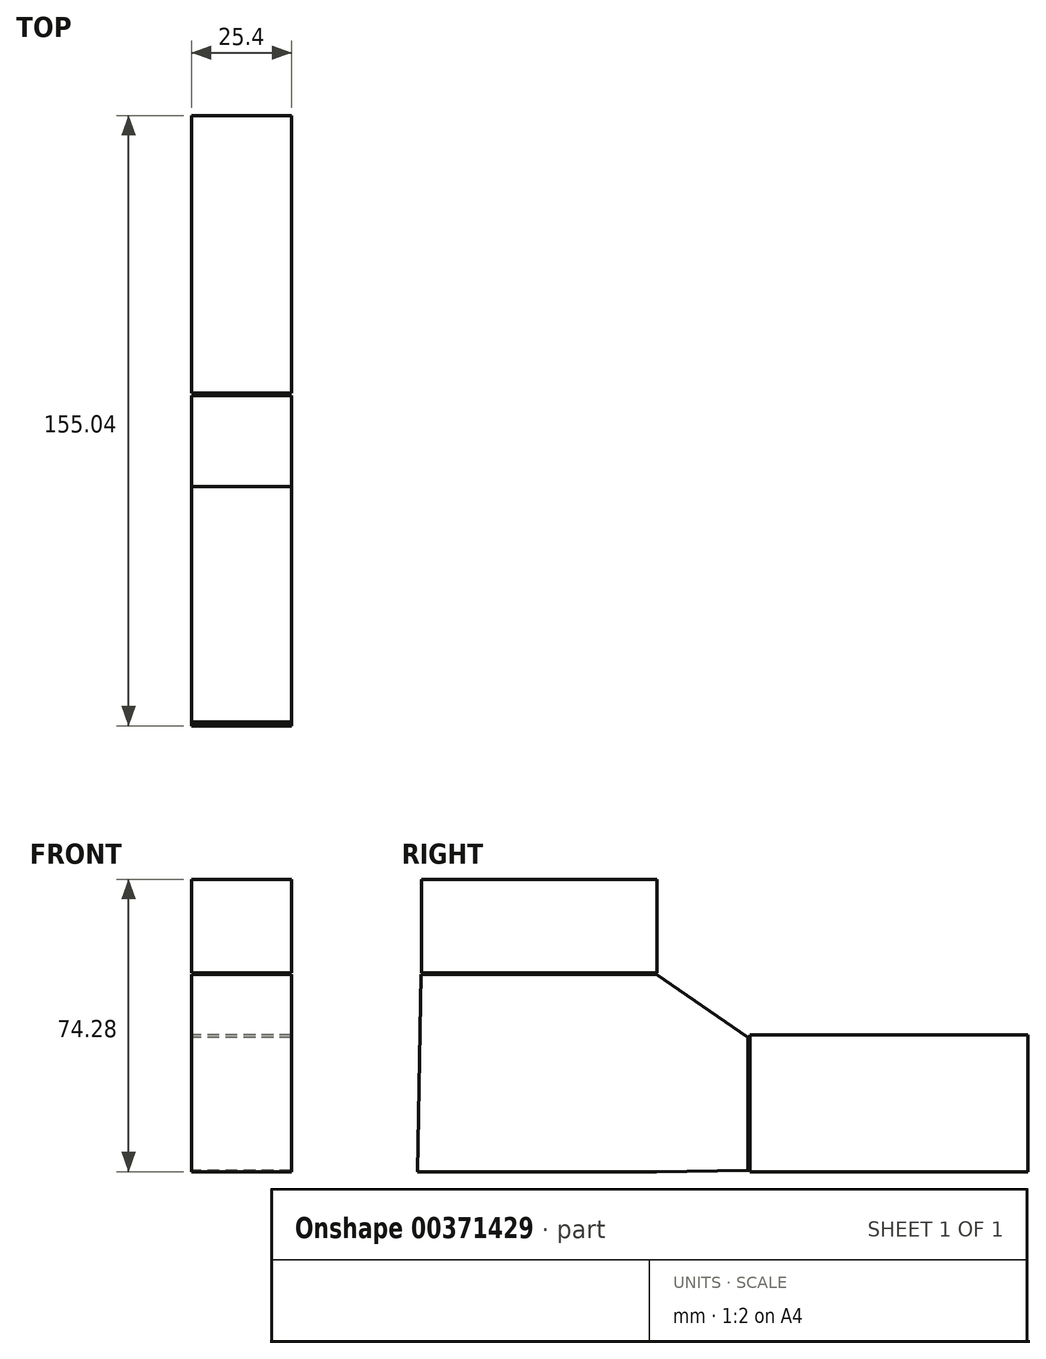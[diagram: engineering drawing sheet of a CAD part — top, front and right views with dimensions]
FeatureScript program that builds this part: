
annotation { "Feature Type Name" : "Feature", "Feature Type Description" : "" }
export const myFeature = defineFeature(function(context is Context, id is Id, definition is map)
    precondition{}
    {
        {
            var Q0;
            Q0=qCreatedBy(makeId("Right.planeOp"),FACE);
            var sketch = newSketch(context, id + "F0", { "sketchPlane" : qUnion([Q0])});
            skLineSegment(sketch, "E0.bottom", {"start": v(35.28, 17.35) * mm, "end": v(-35.28, 17.35) * mm});
            skLineSegment(sketch, "E0.top", {"start": v(35.28, -17.35) * mm, "end": v(-35.28, -17.35) * mm});
            skLineSegment(sketch, "E0.left", {"start": v(35.28, 17.35) * mm, "end": v(35.28, -17.35) * mm});
            skLineSegment(sketch, "E0.right", {"start": v(-35.28, 17.35) * mm, "end": v(-35.28, -17.35) * mm});
            skPoint(sketch, "E0.middle", {"position": v(0, 0) * mm});
            skLineSegment(sketch, "E1", {"start": v(-35.28, 17.35) * mm, "end": v(-59, 33.18) * mm});
            skLineSegment(sketch, "E2.bottom", {"start": v(-59, 33.18) * mm, "end": v(-118.73, 33.18) * mm});
            skLineSegment(sketch, "E2.top", {"start": v(-59, 56.93) * mm, "end": v(-118.73, 56.93) * mm});
            skLineSegment(sketch, "E2.left", {"start": v(-59, 33.18) * mm, "end": v(-59, 56.93) * mm});
            skLineSegment(sketch, "E2.right", {"start": v(-118.73, 33.18) * mm, "end": v(-118.73, 56.93) * mm});
            skSolve(sketch);
        }
        {
            var Q0;
            Q0=makeQuery(id+"F0.imprint","IMPRINT",FACE,{"disambiguationData":[TD([[makeQuery(id+"F0.imprint","IMPRINT",EDGE,{"derivedFrom":sQuery(id+"F0.wireOp",EDGE,"E2.bottom")}),-1.0]])]});
            var sketch = newSketch(context, id + "F1", { "sketchPlane" : qUnion([Q0])});
            skLineSegment(sketch, "E3", {"start": v(-59.06, 32.73) * mm, "end": v(-59.06, -17.34) * mm});
            skLineSegment(sketch, "E4", {"start": v(-118.92, 32.73) * mm, "end": v(-59.06, -17.34) * mm});
            skLineSegment(sketch, "E5", {"start": v(-35.84, 16.79) * mm, "end": v(-59.06, -17.34) * mm});
            skLineSegment(sketch, "E6", {"start": v(-59.06, 32.73) * mm, "end": v(-119.76, -17.34) * mm});
            skLineSegment(sketch, "E7", {"start": v(-35.84, 16.79) * mm, "end": v(-35.84, -17.07) * mm});
            skLineSegment(sketch, "E8", {"start": v(-35.84, -17.07) * mm, "end": v(-59.06, -17.34) * mm});
            skLineSegment(sketch, "E9", {"start": v(-35.84, 16.79) * mm, "end": v(-59.06, 32.73) * mm});
            skLineSegment(sketch, "E10", {"start": v(-59.06, 32.73) * mm, "end": v(-118.92, 32.73) * mm});
            skLineSegment(sketch, "E11", {"start": v(-118.92, 32.73) * mm, "end": v(-119.76, -17.34) * mm});
            skLineSegment(sketch, "E12", {"start": v(-119.76, -17.34) * mm, "end": v(-59.06, -17.34) * mm});
            skSolve(sketch);
        }
        {
            var Q0;
            Q0=makeQuery(id+"F1.imprint","IMPRINT",FACE,{"disambiguationData":[TD([[makeQuery(id+"F1.imprint","IMPRINT",EDGE,{"derivedFrom":makeQuery(id+"F0.imprint","IMPRINT",EDGE,{"derivedFrom":sQuery(id+"F0.wireOp",EDGE,"E2.bottom")})}),-1.0]])]});
            var Q1;
            {var subQ0=sQuery(id+"F1.wireOp",EDGE,"E10");Q1=makeQuery(id+"F1.imprint","IMPRINT",FACE,{"disambiguationData":[TD([[makeQuery(id+"F1.imprint","IMPRINT",EDGE,{"derivedFrom":subQ0}),1.0]])]});}
            var Q2;
            {var subQ0=sQuery(id+"F1.wireOp",EDGE,"E11");Q2=makeQuery(id+"F1.imprint","IMPRINT",FACE,{"disambiguationData":[TD([[makeQuery(id+"F1.imprint","IMPRINT",EDGE,{"derivedFrom":subQ0}),1.0]])]});}
            var Q3;
            {var subQ0=sQuery(id+"F1.wireOp",EDGE,"E12");Q3=makeQuery(id+"F1.imprint","IMPRINT",FACE,{"disambiguationData":[TD([[makeQuery(id+"F1.imprint","IMPRINT",EDGE,{"derivedFrom":subQ0}),1.0]])]});}
            var Q4;
            {var subQ0=sQuery(id+"F1.wireOp",EDGE,"E3");Q4=makeQuery(id+"F1.imprint","IMPRINT",FACE,{"disambiguationData":[TD([[makeQuery(id+"F1.imprint","IMPRINT",EDGE,{"derivedFrom":subQ0}),-1.0]])]});}
            var Q5;
            Q5=makeQuery(id+"F1.imprint","IMPRINT",FACE,{"disambiguationData":[TD([[makeQuery(id+"F1.imprint","IMPRINT",EDGE,{"derivedFrom":sQuery(id+"F1.wireOp",EDGE,"E3")}),1.0]])]});
            var Q6;
            Q6=makeQuery(id+"F1.imprint","IMPRINT",FACE,{"disambiguationData":[TD([[makeQuery(id+"F1.imprint","IMPRINT",EDGE,{"derivedFrom":sQuery(id+"F1.wireOp",EDGE,"E5")}),1.0]])]});
            var Q7;
            Q7=makeQuery(id+"F0.imprint","IMPRINT",FACE,{"disambiguationData":[TD([[makeQuery(id+"F0.imprint","IMPRINT",EDGE,{"derivedFrom":sQuery(id+"F0.wireOp",EDGE,"E0.bottom")}),1.0]])]});
            extrude(context, id + "F2", {"entities" : qUnion([Q0, Q1, Q2, Q3, Q4, Q5, Q6, Q7]), "depth" : 25.4 * mm});
        }
    });
